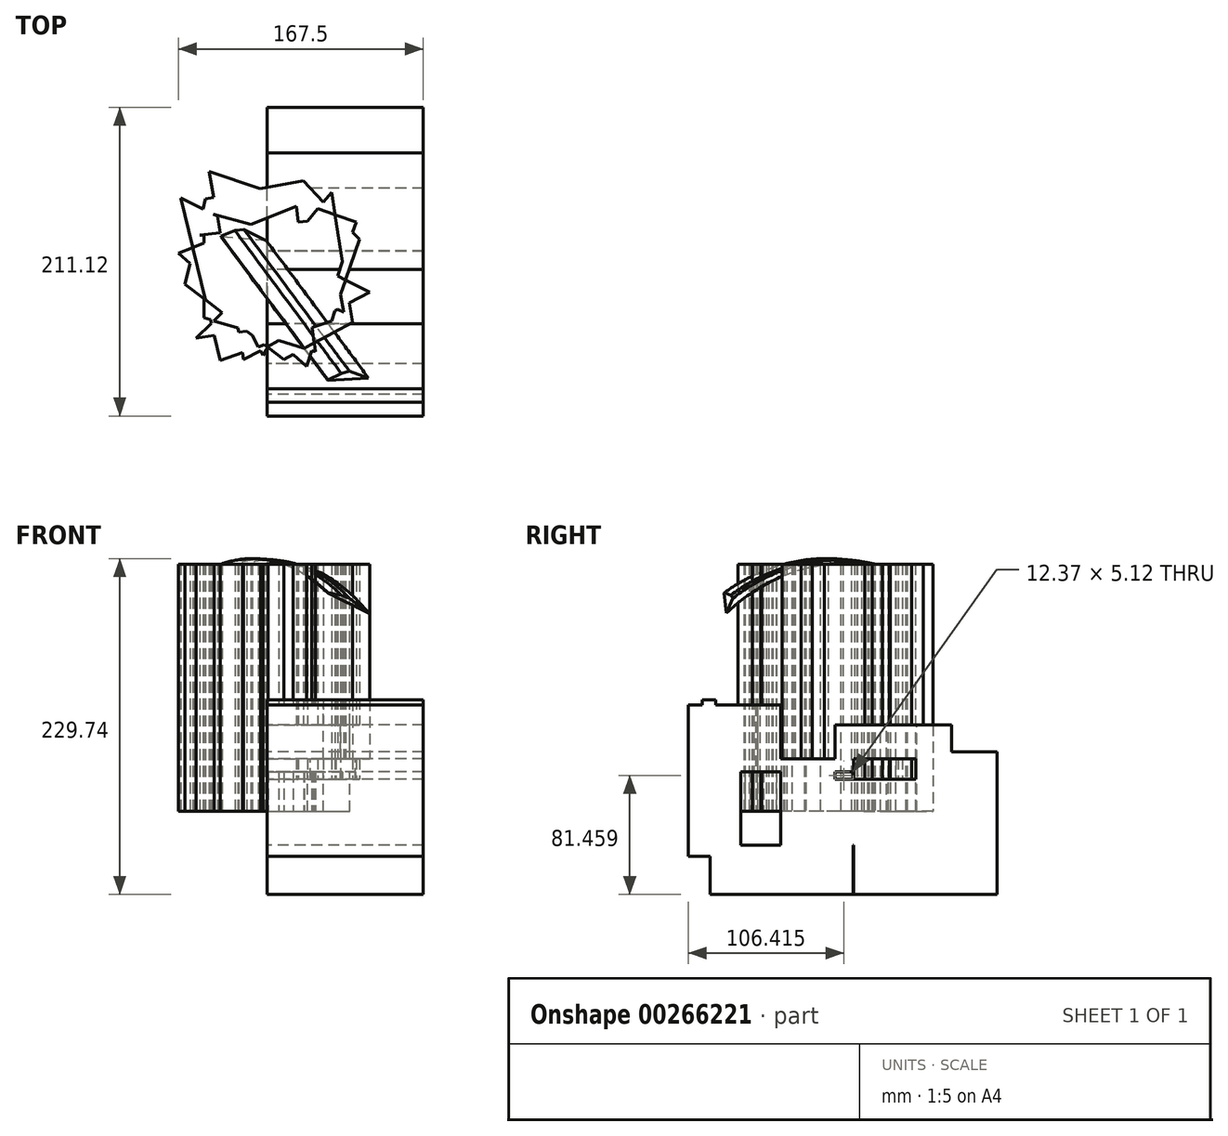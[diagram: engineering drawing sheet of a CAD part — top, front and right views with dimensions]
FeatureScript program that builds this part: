
annotation { "Feature Type Name" : "Feature", "Feature Type Description" : "" }
export const myFeature = defineFeature(function(context is Context, id is Id, definition is map)
    precondition{}
    {
        {
            var Q0;
            Q0=qCreatedBy(makeId("Top.planeOp"),FACE);
            var sketch = newSketch(context, id + "F0", { "sketchPlane" : qUnion([Q0])});
            skLineSegment(sketch, "E0", {"start": v(0, 0) * mm, "end": v(-48.82, -46.86) * mm});
            skLineSegment(sketch, "E1", {"start": v(-48.82, -46.86) * mm, "end": v(16.45, -38.24) * mm});
            skLineSegment(sketch, "E2", {"start": v(16.45, -38.24) * mm, "end": v(29.5, 17.36) * mm});
            skLineSegment(sketch, "E3", {"start": v(29.5, 17.36) * mm, "end": v(-46.2, 23.36) * mm});
            skLineSegment(sketch, "E4", {"start": v(-46.2, 23.36) * mm, "end": v(40.46, 34.85) * mm});
            skLineSegment(sketch, "E5", {"start": v(40.46, 34.85) * mm, "end": v(52.2, -29.1) * mm});
            skLineSegment(sketch, "E6", {"start": v(52.2, -29.1) * mm, "end": v(-44.12, 17.36) * mm});
            skLineSegment(sketch, "E7", {"start": v(-44.12, 17.36) * mm, "end": v(-2.87, -58.62) * mm});
            skLineSegment(sketch, "E8", {"start": v(-2.87, -58.62) * mm, "end": v(43.9, 16.12) * mm});
            skLineSegment(sketch, "E9", {"start": v(43.9, 16.12) * mm, "end": v(-43.33, 39.6) * mm});
            skLineSegment(sketch, "E10", {"start": v(-43.33, 39.6) * mm, "end": v(-43.33, -33.02) * mm});
            skLineSegment(sketch, "E11", {"start": v(-43.33, -33.02) * mm, "end": v(32.9, -56.27) * mm});
            skLineSegment(sketch, "E12", {"start": v(32.9, -56.27) * mm, "end": v(19.84, 43.26) * mm});
            skLineSegment(sketch, "E13", {"start": v(19.84, 43.26) * mm, "end": v(-60.82, 11.13) * mm});
            skLineSegment(sketch, "E14", {"start": v(-60.82, 11.13) * mm, "end": v(26.89, -66.2) * mm});
            skLineSegment(sketch, "E15", {"start": v(26.89, -66.2) * mm, "end": v(60.82, 32.55) * mm});
            skLineSegment(sketch, "E16", {"start": v(60.82, 32.55) * mm, "end": v(-39.74, 67.1) * mm});
            skLineSegment(sketch, "E17", {"start": v(-39.74, 67.1) * mm, "end": v(-16.1, -61.55) * mm});
            skLineSegment(sketch, "E18", {"start": v(-16.1, -61.55) * mm, "end": v(69.96, -15.52) * mm});
            skLineSegment(sketch, "E19", {"start": v(69.96, -15.52) * mm, "end": v(-59.26, 49) * mm});
            skLineSegment(sketch, "E20", {"start": v(-59.26, 49) * mm, "end": v(-32.1, -62.28) * mm});
            skLineSegment(sketch, "E21", {"start": v(-32.1, -62.28) * mm, "end": v(43.9, -35.1) * mm});
            skLineSegment(sketch, "E22", {"start": v(43.9, -35.1) * mm, "end": v(63.04, 20.57) * mm});
            skLineSegment(sketch, "E23", {"start": v(63.04, 20.57) * mm, "end": v(24.65, 60.56) * mm});
            skLineSegment(sketch, "E24", {"start": v(24.65, 60.56) * mm, "end": v(-42.41, 48.24) * mm});
            skLineSegment(sketch, "E25", {"start": v(-42.41, 48.24) * mm, "end": v(-56.12, -10.17) * mm});
            skLineSegment(sketch, "E26", {"start": v(-56.12, -10.17) * mm, "end": v(11.22, -61.5) * mm});
            skLineSegment(sketch, "E27", {"start": v(11.22, -61.5) * mm, "end": v(58.21, -36.15) * mm});
            skLineSegment(sketch, "E28", {"start": v(58.21, -36.15) * mm, "end": v(43.9, 52.66) * mm});
            skLineSegment(sketch, "E29", {"start": v(43.9, 52.66) * mm, "end": v(0, 0) * mm});
            skSolve(sketch);
        }
        {
            var Q0;
            Q0 = qSketchRegion(id + "F0", true);
            var Q1;
            {var subQ1=sQuery(id+"F0.wireOp",EDGE,"E4");var subQ5=sQuery(id+"F0.wireOp",EDGE,"E10");var subQ8=makeQuery(id+"F0.imprint","INTERSECT",VERTEX,{"derivedFrom":[subQ1,subQ5]});Q1=makeQuery(id+"F0.imprint","IMPRINT",FACE,{"disambiguationData":[TD([[makeQuery(id+"F0.imprint","IMPRINT",EDGE,{"disambiguationData":[TD([[subQ8,-1.0]])],"derivedFrom":subQ1}),1.0]])]});}
            var Q2;
            {var subQ5=sQuery(id+"F0.wireOp",EDGE,"E19");var subQ7=sQuery(id+"F0.wireOp",EDGE,"E3");var subQ8=makeQuery(id+"F0.imprint","INTERSECT",VERTEX,{"derivedFrom":[subQ7,subQ5]});Q2=makeQuery(id+"F0.imprint","IMPRINT",FACE,{"disambiguationData":[TD([[makeQuery(id+"F0.imprint","IMPRINT",EDGE,{"disambiguationData":[TD([[subQ8,-1.0]])],"derivedFrom":subQ7}),-1.0]])]});}
            extrude(context, id + "F1", {"entities" : qUnion([Q0, Q1, Q2]), "depth" : 169.16 * mm});
        }
        {
            var Q0;
            Q0=qCreatedBy(makeId("Top.planeOp"),FACE);
            var sketch = newSketch(context, id + "F2", { "sketchPlane" : qUnion([Q0])});
            skLineSegment(sketch, "E30", {"start": v(-19.58, -12.92) * mm, "end": v(23.23, 18.93) * mm});
            skSolve(sketch);
        }
        {
            var Q0;
            Q0=makeQuery(id+"F1.opExtrude","CAP_FACE",FACE,{"disambiguationData":[OSD([sQuery(id+"F0.wireOp",EDGE,"E3"),sQuery(id+"F0.wireOp",EDGE,"E4"),sQuery(id+"F0.wireOp",EDGE,"E13"),sQuery(id+"F0.wireOp",EDGE,"E17"),sQuery(id+"F0.wireOp",EDGE,"E19")])],"isStart":false});
            var Q1;
            Q1=sQuery(id+"F2.wireOp",EDGE,"E30");
            revolve(context, id + "F3", {"entities" : qUnion([Q0]), "axis" : qUnion([Q1]), "revolveType" : RevolveType.ONE_DIRECTION, "angle" : 42 * degree});
        }
        {
            var Q0;
            Q0=qCreatedBy(makeId("Right.planeOp"),FACE);
            var sketch = newSketch(context, id + "F4", { "sketchPlane" : qUnion([Q0])});
            skLineSegment(sketch, "E31.bottom", {"start": v(-85.3, 27.19) * mm, "end": v(12.37, 27.19) * mm});
            skLineSegment(sketch, "E31.top", {"start": v(-85.3, -56.83) * mm, "end": v(12.37, -56.83) * mm});
            skLineSegment(sketch, "E31.left", {"start": v(-85.3, 27.19) * mm, "end": v(-85.3, -56.83) * mm});
            skLineSegment(sketch, "E31.right", {"start": v(12.37, 27.19) * mm, "end": v(12.37, -56.83) * mm});
            skLineSegment(sketch, "E32.bottom", {"start": v(12.8, -56.83) * mm, "end": v(110.9, -56.83) * mm});
            skLineSegment(sketch, "E32.top", {"start": v(12.8, 40.84) * mm, "end": v(110.9, 40.84) * mm});
            skLineSegment(sketch, "E32.left", {"start": v(12.8, -56.83) * mm, "end": v(12.8, 40.84) * mm});
            skLineSegment(sketch, "E32.right", {"start": v(110.9, -56.83) * mm, "end": v(110.9, 40.84) * mm});
            skLineSegment(sketch, "E33.bottom", {"start": v(79.76, 59.18) * mm, "end": v(0, 59.18) * mm});
            skLineSegment(sketch, "E33.top", {"start": v(79.76, 22.07) * mm, "end": v(0, 22.07) * mm});
            skLineSegment(sketch, "E33.left", {"start": v(79.76, 59.18) * mm, "end": v(79.76, 22.07) * mm});
            skLineSegment(sketch, "E33.right", {"start": v(0, 59.18) * mm, "end": v(0, 22.07) * mm});
            skLineSegment(sketch, "E34.bottom", {"start": v(-90.85, 76.24) * mm, "end": v(-81.46, 76.24) * mm});
            skLineSegment(sketch, "E34.top", {"start": v(-90.85, 68.13) * mm, "end": v(-81.46, 68.13) * mm});
            skLineSegment(sketch, "E34.left", {"start": v(-90.85, 76.24) * mm, "end": v(-90.85, 68.13) * mm});
            skLineSegment(sketch, "E34.right", {"start": v(-81.46, 76.24) * mm, "end": v(-81.46, 68.13) * mm});
            skLineSegment(sketch, "E35.bottom", {"start": v(-37.1, -30.82) * mm, "end": v(-100.23, -30.82) * mm});
            skLineSegment(sketch, "E35.top", {"start": v(-37.1, 72.83) * mm, "end": v(-100.23, 72.83) * mm});
            skLineSegment(sketch, "E35.left", {"start": v(-37.1, -30.82) * mm, "end": v(-37.1, 72.83) * mm});
            skLineSegment(sketch, "E35.right", {"start": v(-100.23, -30.82) * mm, "end": v(-100.23, 72.83) * mm});
            skLineSegment(sketch, "E36.bottom", {"start": v(55.45, -23.14) * mm, "end": v(-64.4, -23.14) * mm});
            skLineSegment(sketch, "E36.top", {"start": v(55.45, 36.15) * mm, "end": v(-64.4, 36.15) * mm});
            skLineSegment(sketch, "E36.left", {"start": v(55.45, -23.14) * mm, "end": v(55.45, 36.15) * mm});
            skLineSegment(sketch, "E36.right", {"start": v(-64.4, -23.14) * mm, "end": v(-64.4, 36.15) * mm});
            skSolve(sketch);
        }
        {
            var Q0;
            Q0 = qSketchRegion(id + "F4", true);
            extrude(context, id + "F5", {"entities" : qUnion([Q0]), "operationType" : NewBodyOperationType.ADD, "depth" : 106.68 * mm});
        }
    });
